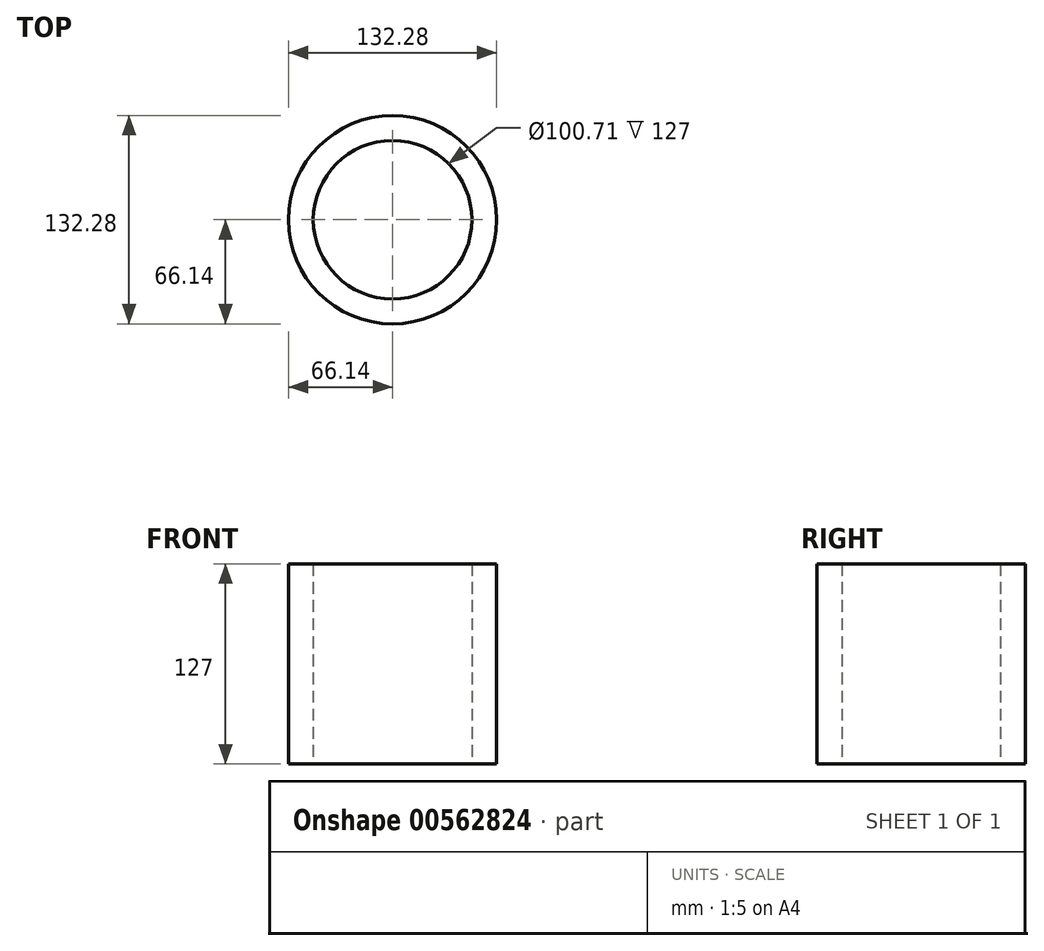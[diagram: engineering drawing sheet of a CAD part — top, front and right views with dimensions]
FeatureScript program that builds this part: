
annotation { "Feature Type Name" : "Feature", "Feature Type Description" : "" }
export const myFeature = defineFeature(function(context is Context, id is Id, definition is map)
    precondition{}
    {
        {
            var Q0;
            Q0=qCreatedBy(makeId("Top.planeOp"),FACE);
            var sketch = newSketch(context, id + "F0", { "sketchPlane" : qUnion([Q0])});
            skCircle(sketch, "E0", {"center": v(0, 0) * mm, "radius": 66.14 * mm});
            skCircle(sketch, "E1", {"center": v(0, 0) * mm, "radius": 50.35 * mm});
            skSolve(sketch);
        }
        {
            var Q0;
            Q0=makeQuery(id+"F0.imprint","IMPRINT",FACE,{"disambiguationData":[TD([[makeQuery(id+"F0.imprint","IMPRINT",EDGE,{"derivedFrom":sQuery(id+"F0.wireOp",EDGE,"E0")}),1.0]])]});
            extrude(context, id + "F1", {"entities" : qUnion([Q0]), "depth" : 127 * mm, "offsetDistance" : 25.4 * mm});
        }
    });
